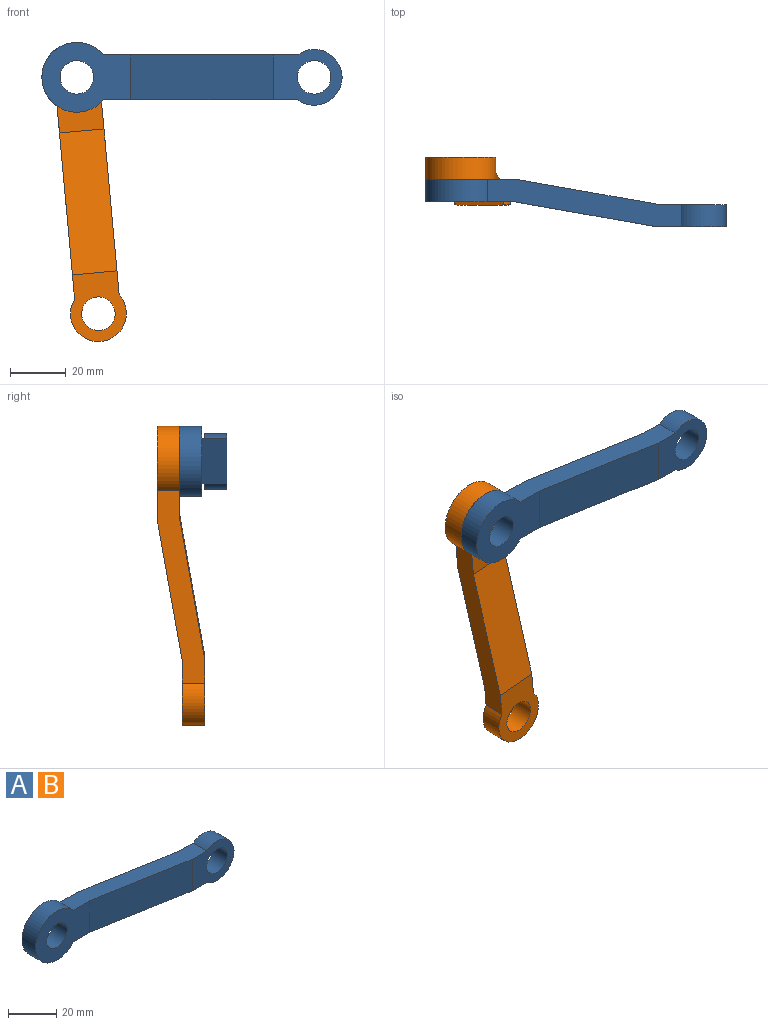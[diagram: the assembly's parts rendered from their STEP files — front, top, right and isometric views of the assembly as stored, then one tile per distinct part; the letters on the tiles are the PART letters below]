
ASSEMBLY  parts=2 mates=1
PART A: 12 faces, bbox 107.5x17x25 mm
  f0: cylinder r=6mm len=12mm, axis (0,1,0), area 301.6mm2, adj f1,f4
  f1: plane 24.66x20mm, normal (0,-1,0), area 294.9mm2, adj f0,f3,f6,f7,f8
  f2: plane 31.8x25mm, normal (0,-1,0), area 501.2mm2, adj f3,f6,f8,f9,f10
  f3: plane 51.04x16mm, normal (-0.17,-0.98,0), area 829.3mm2, adj f1,f2,f6,f8
  f4: plane 23.96x20mm, normal (0,1,0), area 283.7mm2, adj f0,f5,f6,f7,f8
  f5: plane 51.04x16mm, normal (0.17,0.98,0), area 829.3mm2, adj f4,f6,f8,f11
  f6: plane 69.4x17mm, normal (0,0,-1), area 561.5mm2, adj f1,f2,f3,f4,f5,f7,f9,f11
  f7: cylinder r=10mm len=20mm, axis (0,1,0), area 354.3mm2, adj f1,f4,f6,f8
  f8: plane 69.4x17mm, normal (0,0,1), area 561.5mm2, adj f1,f2,f3,f4,f5,f7,f9,f11
  f9: cylinder r=12.5mm len=25mm, axis (0,1,0), area 489.4mm2, adj f2,f6,f8,f11
  f10: cylinder r=6mm len=12mm, axis (0,1,0), area 301.6mm2, adj f2,f11
  f11: plane 32.5x25mm, normal (0,1,0), area 512.4mm2, adj f5,f6,f8,f9,f10
PART B: same geometry as A
PLACE A t=(-39.45,-30.88,29.37)mm fixed
PLACE B rot(axis=(0,1,0),84.8deg) t=(-39.45,-22.88,29.37)mm
MATE revolute B.f10 <-> A.f10  axis (0,-1,0) through (-39.45,-30.88,29.37)mm
